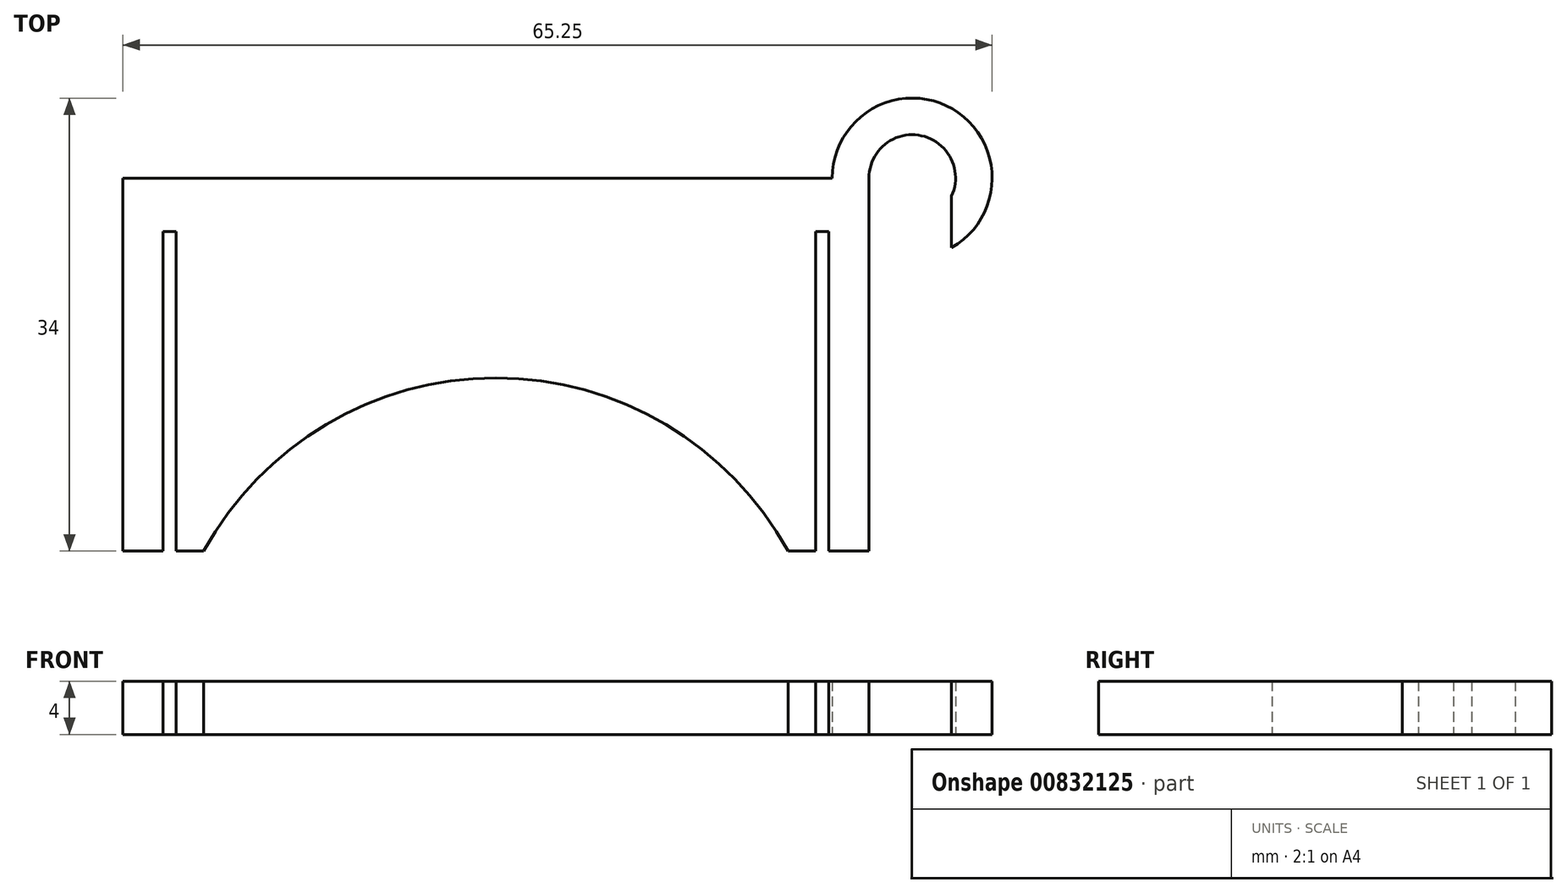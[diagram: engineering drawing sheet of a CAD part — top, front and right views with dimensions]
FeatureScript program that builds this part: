
annotation { "Feature Type Name" : "Feature", "Feature Type Description" : "" }
export const myFeature = defineFeature(function(context is Context, id is Id, definition is map)
    precondition{}
    {
        {
            var Q0;
            Q0=qCreatedBy(makeId("Top.planeOp"),FACE);
            var sketch = newSketch(context, id + "F0", { "sketchPlane" : qUnion([Q0])});
            skLineSegment(sketch, "E0", {"start": v(-28, -28) * mm, "end": v(-25, -28) * mm});
            skLineSegment(sketch, "E1", {"start": v(-25, -28) * mm, "end": v(-25, -4) * mm});
            skLineSegment(sketch, "E2", {"start": v(-25, -4) * mm, "end": v(-24, -4) * mm});
            skLineSegment(sketch, "E3", {"start": v(-24, -4) * mm, "end": v(-24, -28) * mm});
            skLineSegment(sketch, "E4", {"start": v(-24, -28) * mm, "end": v(-21.93, -28) * mm});
            skLineSegment(sketch, "E5.MirrorCS", {"start": v(25, -4) * mm, "end": v(24, -4) * mm});
            skLineSegment(sketch, "E6.MirrorCS", {"start": v(28, -28) * mm, "end": v(25, -28) * mm});
            skLineSegment(sketch, "E7.MirrorCS", {"start": v(24, -28) * mm, "end": v(21.93, -28) * mm});
            skLineSegment(sketch, "E8.MirrorCS", {"start": v(24, -4) * mm, "end": v(24, -28) * mm});
            skLineSegment(sketch, "E9.MirrorCS", {"start": v(25, -28) * mm, "end": v(25, -4) * mm});
            skArc(sketch, "E10", {"start": v(21.93, -28) * mm, "mid": v(0, -15) * mm, "end": v(-21.93, -28) * mm});
            skLineSegment(sketch, "E11", {"start": v(-28, -28) * mm, "end": v(-28, 0) * mm});
            skLineSegment(sketch, "E12", {"start": v(-28, 0) * mm, "end": v(0, 0) * mm});
            skLineSegment(sketch, "E13.MirrorCS", {"start": v(28, 0) * mm, "end": v(0, 0) * mm});
            skLineSegment(sketch, "E14.MirrorCS", {"start": v(28, -28) * mm, "end": v(28, 0) * mm});
            skArc(sketch, "E15", {"start": v(34.2, -1.36) * mm, "mid": v(31.95, 3.17) * mm, "end": v(28, 0) * mm});
            skArc(sketch, "E16", {"start": v(34.2, -5.22) * mm, "mid": v(34.27, 5.18) * mm, "end": v(25.25, 0) * mm});
            skLineSegment(sketch, "E17", {"start": v(34.2, -1.36) * mm, "end": v(34.2, -5.22) * mm});
            skSolve(sketch);
        }
        {
            var Q0;
            Q0=makeQuery(id+"F0.imprint","IMPRINT",FACE,{"disambiguationData":[TD([[makeQuery(id+"F0.imprint","IMPRINT",EDGE,{"derivedFrom":sQuery(id+"F0.wireOp",EDGE,"E0")}),1.0]])]});
            var Q1;
            {var subQ0=sQuery(id+"F0.wireOp",EDGE,"E15");Q1=makeQuery(id+"F0.imprint","IMPRINT",FACE,{"disambiguationData":[TD([[makeQuery(id+"F0.imprint","IMPRINT",EDGE,{"derivedFrom":subQ0}),-1.0]])]});}
            extrude(context, id + "F1", {"entities" : qUnion([Q0, Q1]), "endBound" : BoundingType.SYMMETRIC, "depth" : 4 * mm, "offsetDistance" : 25.4 * mm});
        }
    });
